# Revit family: Sanitary_Toilets_hansgrohe_60312XXX-GladeLake-S-Floorstanding-WC-Set_640_AquaChannel-Flush_tank-WC-seat-cover
name_source: partatom
category: Plumbing Fixtures
units: mm (PartAtom-declared; Revit-internal decimal feet)

## family parameters
Always vertical = Yes
Cut with Voids When Loaded = No
Maintain Annotation Orientation = No
OmniClass Number = 23.31.19.00
OmniClass Title = Toilets
Part Type = Normal
Room Calculation Point = No
Round Connector Dimension = Use Diameter
Shared = No
Work Plane-Based = Yes

## types (1)
- 450 White
    Connector Description = Water Outlet 102mm
    Date Updated = 2025/01/09
    Default Elevation = 0 mm  [stored 0 ft]
    Description = GladeLake S Floorstanding WC Set close coupled 640 with horizontal/vertical outlet AquaChannel Flush with tank and WC seat and cover
    Diameter = 102 mm
    Inlet Connector Description = Water Inlet 12.7 mm
    Manufacturer = Hansgrohe
    Material 1 = Hansgrohe - Ceramic - 450 White
    Material 2 = Hansgrohe - Metal - Black
    Model = 60312XXX
    Product Page URL = https://www.hansgrohe.com
    Product data url = https://www.bimobject.com
    URL = https://www.hansgrohe.com
    Version = 1

note: [stored X ft] marks values corroborated as IEEE doubles in the binary element streams (Revit-internal decimal feet)

## geometry (parser evidence)
native form markers: Sweep x2
no freeform markers — native parametric forms only
